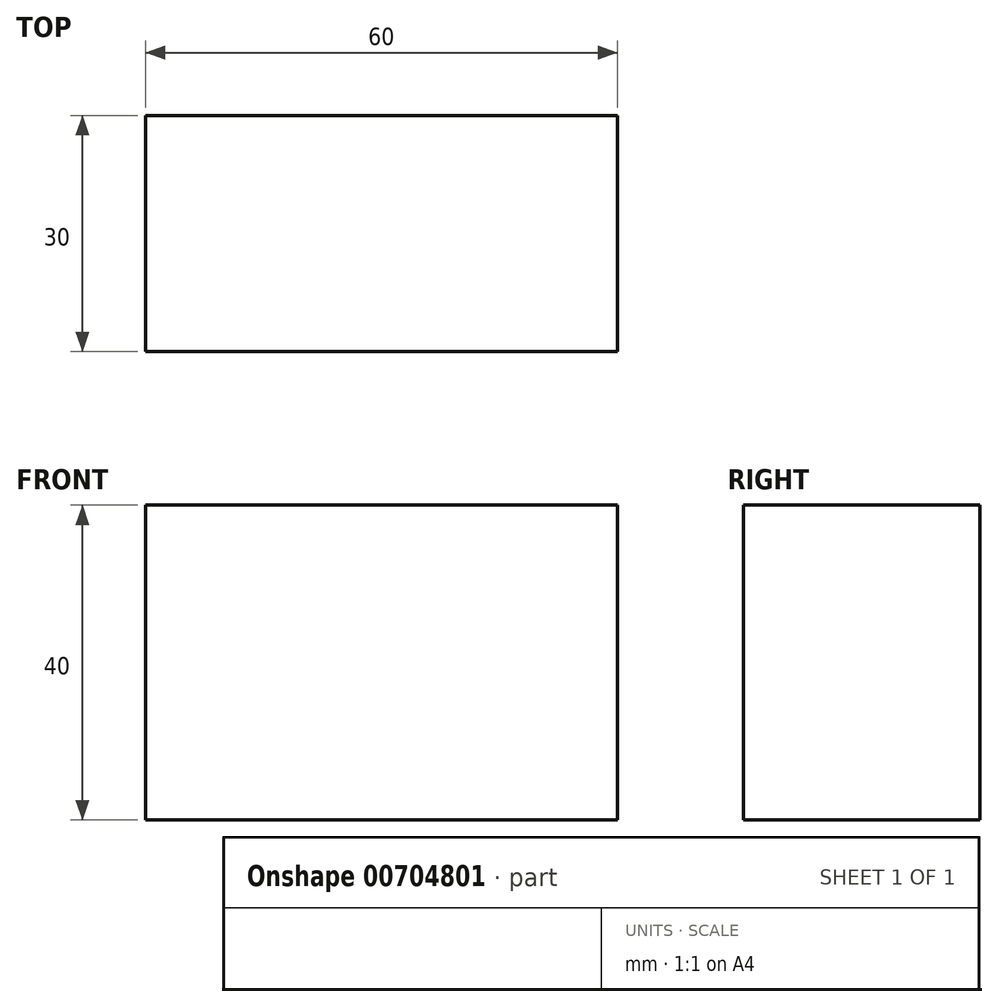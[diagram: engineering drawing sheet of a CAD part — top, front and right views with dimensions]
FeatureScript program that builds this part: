
annotation { "Feature Type Name" : "Feature", "Feature Type Description" : "" }
export const myFeature = defineFeature(function(context is Context, id is Id, definition is map)
    precondition{}
    {
        {
            var Q0;
            Q0=qCreatedBy(makeId("Front.planeOp"),FACE);
            var sketch = newSketch(context, id + "F0", { "sketchPlane" : qUnion([Q0])});
            skLineSegment(sketch, "E0.bottom", {"start": v(0, 0) * mm, "end": v(-60, 0) * mm});
            skLineSegment(sketch, "E0.top", {"start": v(0, 40) * mm, "end": v(-60, 40) * mm});
            skLineSegment(sketch, "E0.left", {"start": v(0, 0) * mm, "end": v(0, 40) * mm});
            skLineSegment(sketch, "E0.right", {"start": v(-60, 0) * mm, "end": v(-60, 40) * mm});
            skSolve(sketch);
        }
        {
            var Q0;
            Q0=makeQuery(id+"F0.imprint","IMPRINT",FACE,{"disambiguationData":[TD([[makeQuery(id+"F0.imprint","IMPRINT",EDGE,{"derivedFrom":sQuery(id+"F0.wireOp",EDGE,"E0.bottom")}),-1.0]])]});
            extrude(context, id + "F1", {"entities" : qUnion([Q0]), "depth" : 30 * mm, "offsetDistance" : 25 * mm});
        }
    });
